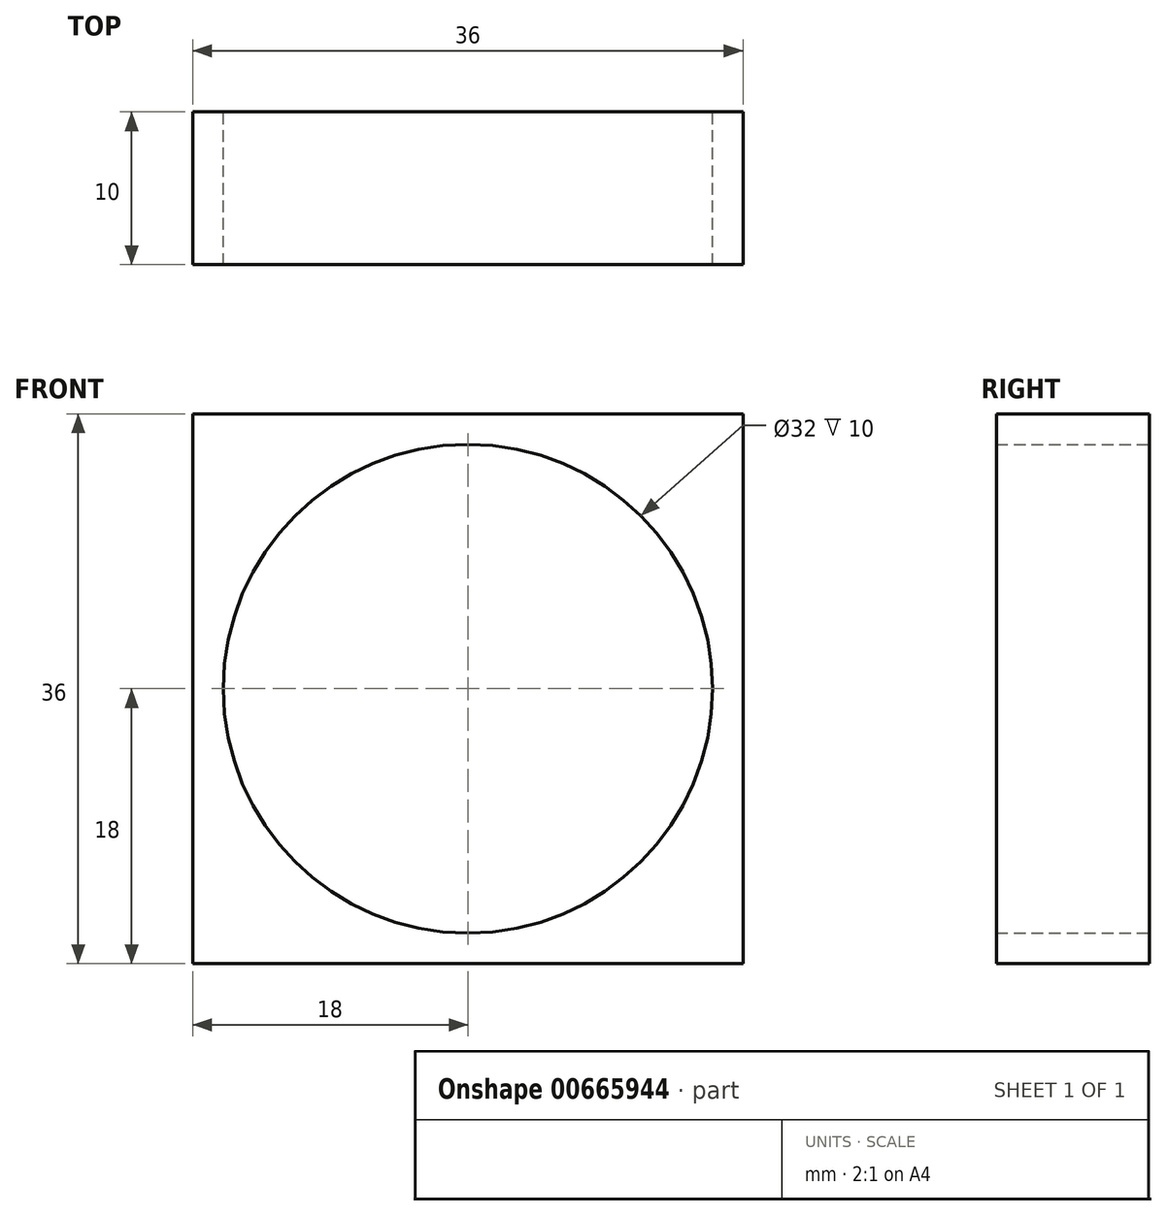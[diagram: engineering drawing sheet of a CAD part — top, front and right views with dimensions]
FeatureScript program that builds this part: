
annotation { "Feature Type Name" : "Feature", "Feature Type Description" : "" }
export const myFeature = defineFeature(function(context is Context, id is Id, definition is map)
    precondition{}
    {
        {
            var Q0;
            Q0=qCreatedBy(makeId("Front.planeOp"),FACE);
            var sketch = newSketch(context, id + "F0", { "sketchPlane" : qUnion([Q0])});
            skLineSegment(sketch, "E0.bottom", {"start": v(18, 18) * mm, "end": v(-18, 18) * mm});
            skLineSegment(sketch, "E0.top", {"start": v(18, -18) * mm, "end": v(-18, -18) * mm});
            skLineSegment(sketch, "E0.left", {"start": v(18, 18) * mm, "end": v(18, -18) * mm});
            skLineSegment(sketch, "E0.right", {"start": v(-18, 18) * mm, "end": v(-18, -18) * mm});
            skPoint(sketch, "E0.middle", {"position": v(0, 0) * mm});
            skCircle(sketch, "E1", {"center": v(0, 0) * mm, "radius": 16 * mm});
            skSolve(sketch);
        }
        {
            var Q0;
            Q0 = qSketchRegion(id + "F0", true);
            extrude(context, id + "F1", {"entities" : qUnion([Q0]), "depth" : 10 * mm, "offsetDistance" : 25 * mm});
        }
    });
